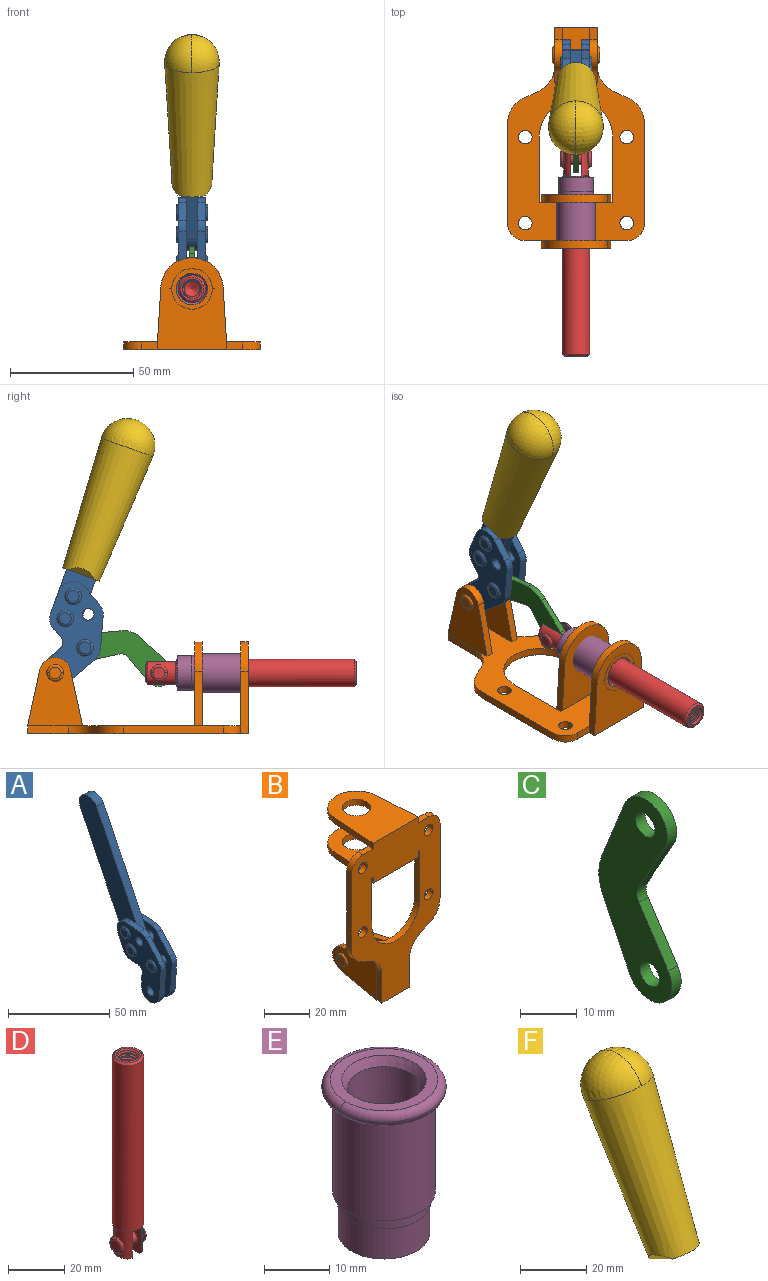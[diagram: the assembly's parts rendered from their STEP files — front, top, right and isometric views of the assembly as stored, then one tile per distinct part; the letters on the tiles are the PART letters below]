
ASSEMBLY  parts=6 mates=6
PART A: 59 faces, bbox 12.9x60.2x99.6 mm
  f0: torus R=2.39mm, axis (-1,0,0), area 14.9mm2, adj f20,f43,f51
  f1: torus R=2.39mm, axis (-1,0,0), area 14.9mm2, adj f19,f42,f51
  f2: torus R=2.39mm, axis (-1,0,0), area 14.9mm2, adj f18,f35,f51
  f3: torus R=2.39mm, axis (-1,0,0), area 14.9mm2, adj f14,f17,f23
  f4: torus R=2.39mm, axis (-1,0,0), area 14.9mm2, adj f13,f16,f23
  f5: torus R=2.39mm, axis (-1,0,0), area 14.9mm2, adj f12,f15,f23
  f6: cylinder r=2.39mm len=4.78mm, axis (1,0,0), area 46.5mm2, adj f48,f50,f51
  f7: cylinder r=2.39mm len=4.78mm, axis (1,0,0), area 46.5mm2, adj f50,f51
  f8: cylinder r=6.35mm len=12.68mm, axis (1,0,0), area 61.8mm2, adj f38,f39,f50,f51
  f9: cylinder r=2.39mm len=4.78mm, axis (-1,0,0), area 70.5mm2, adj f46,f50
  f10: cylinder r=2.39mm len=4.78mm, axis (-1,0,0), area 46.5mm2, adj f23,f45,f46
  f11: cylinder r=2.39mm len=4.78mm, axis (-1,0,0), area 46.5mm2, adj f23,f46
  f12: plane 4.78x4.78mm, normal (1,0,0), area 17.9mm2, adj f5,f15
  f13: plane 4.78x4.78mm, normal (1,0,0), area 17.9mm2, adj f4,f16
  f14: plane 4.78x4.78mm, normal (1,0,0), area 17.9mm2, adj f3,f17
  f15: torus R=2.39mm, axis (-1,0,0), area 14.9mm2, adj f5,f12,f23
  f16: torus R=2.39mm, axis (-1,0,0), area 14.9mm2, adj f4,f13,f23
  f17: torus R=2.39mm, axis (-1,0,0), area 14.9mm2, adj f3,f14,f23
  f18: plane 4.78x4.78mm, normal (-1,0,0), area 17.9mm2, adj f2,f35
  f19: plane 4.78x4.78mm, normal (-1,0,0), area 17.9mm2, adj f1,f42
  f20: plane 4.78x4.78mm, normal (-1,0,0), area 17.9mm2, adj f0,f43
  f21: plane 2.26x0.2mm, normal (1,0,0), area 0.2mm2, adj f31,f44
  f22: plane 2.26x0.2mm, normal (-1,0,0), area 0.2mm2, adj f41,f44
  f23: plane 39.37x30.77mm, normal (1,0,0), area 565.5mm2, adj f3,f4,f5,f10,f11,f15,f16,f17
  f24: cylinder r=6.1mm len=4.15mm, axis (-1,0,0), area 14.7mm2, adj f23,f25,f32,f46
  f25: plane 10.25x9.01mm, normal (0,-0.75,0.66), area 42.3mm2, adj f23,f24,f26,f46
  f26: cylinder r=6.35mm len=4.64mm, axis (-1,0,0), area 15.6mm2, adj f23,f25,f27,f46
  f27: plane 15.84x3.1mm, normal (0,-1,-0.07), area 49.2mm2, adj f23,f26,f28,f46
  f28: cylinder r=6.35mm len=12.68mm, axis (-1,0,0), area 61.8mm2, adj f23,f27,f29,f46
  f29: plane 8.11x3.1mm, normal (0,1,0.07), area 25.2mm2, adj f23,f28,f30,f46
  f30: cylinder r=3.05mm len=3.25mm, axis (-1,0,0), area 14.8mm2, adj f23,f29,f31,f46
  f31: plane 5.99x3.1mm, normal (0,0.07,-1), area 18.6mm2, adj f21,f23,f30,f44,f46
  f32: plane 9.5x3.1mm, normal (0,-0.07,1), area 29.5mm2, adj f23,f24,f33,f46,f47
  f33: cylinder r=6.1mm len=8.63mm, axis (-1,0,0), area 39.1mm2, adj f23,f32,f34,f47
  f34: plane 8.65x3.96mm, normal (0,0.91,-0.42), area 29.5mm2, adj f23,f33,f44,f47
  f35: torus R=2.39mm, axis (-1,0,0), area 14.9mm2, adj f2,f18,f51
  f36: plane 10.25x9.01mm, normal (0,-0.75,0.66), area 42.3mm2, adj f37,f49,f50,f51
  f37: cylinder r=6.35mm len=4.64mm, axis (1,0,0), area 15.6mm2, adj f36,f38,f50,f51
  f38: plane 15.84x3.1mm, normal (0,-1,-0.07), area 49.2mm2, adj f8,f37,f50,f51
  f39: plane 8.11x3.1mm, normal (0,1,0.07), area 25.2mm2, adj f8,f40,f50,f51
  f40: cylinder r=3.05mm len=3.25mm, axis (1,0,0), area 14.8mm2, adj f39,f41,f50,f51
  f41: plane 5.99x3.1mm, normal (0,0.07,-1), area 18.6mm2, adj f22,f40,f44,f50,f51
  f42: torus R=2.39mm, axis (-1,0,0), area 14.9mm2, adj f1,f19,f51
  f43: torus R=2.39mm, axis (-1,0,0), area 14.9mm2, adj f0,f20,f51
  f44: cylinder r=6.35mm len=12.12mm, axis (-1,0,0), area 128.9mm2, adj f21,f22,f23,f31,f34,f41,f46,f47
  f45: plane 2.65x1.35mm, normal (1,0,0), area 1mm2, adj f10,f55
  f46: plane 39.08x20.42mm, normal (-1,0,0), area 412.5mm2, adj f9,f10,f11,f24,f25,f26,f27,f28
  f47: plane 77.62x39.82mm, normal (1,0,0), area 850mm2, adj f32,f33,f34,f44,f53,f54,f55
  f48: plane 2.65x1.35mm, normal (-1,0,0), area 1mm2, adj f6,f55
  f49: cylinder r=6.1mm len=4.15mm, axis (1,0,0), area 14.7mm2, adj f36,f50,f51,f56
  f50: plane 39.08x20.42mm, normal (1,0,0), area 412.5mm2, adj f6,f7,f8,f9,f36,f37,f38,f39
  f51: plane 39.37x30.77mm, normal (-1,0,0), area 565.5mm2, adj f0,f1,f2,f6,f7,f8,f35,f36
  f52: plane 8.65x3.96mm, normal (0,0.91,-0.42), area 29.5mm2, adj f44,f51,f57,f58
  f53: plane 68.49x33.4mm, normal (0,0.9,-0.44), area 358.1mm2, adj f44,f47,f54,f58
  f54: cylinder r=6.35mm len=12.06mm, axis (1,0,0), area 93.7mm2, adj f47,f53,f55,f58
  f55: plane 68.49x33.4mm, normal (0,-0.9,0.44), area 358.1mm2, adj f44,f45,f46,f47,f48,f50,f54,f58
  f56: plane 9.5x3.1mm, normal (0,-0.07,1), area 29.5mm2, adj f49,f50,f51,f57,f58
  f57: cylinder r=6.1mm len=8.63mm, axis (1,0,0), area 39.1mm2, adj f51,f52,f56,f58
  f58: plane 77.62x39.82mm, normal (-1,0,0), area 850mm2, adj f44,f52,f53,f54,f55,f56,f57
PART B: 55 faces, bbox 55.7x37.4x89.8 mm
  f0: torus R=2.41mm, axis (-1,0,0), area 15mm2, adj f11,f15,f25
  f1: torus R=2.41mm, axis (-1,0,0), area 15mm2, adj f10,f12,f22
  f2: cylinder r=2.78mm len=5.56mm, axis (0,-1,0), area 54.2mm2, adj f30,f54
  f3: cylinder r=14.99mm len=29.97mm, axis (0,-1,0), area 145.9mm2, adj f30,f49,f53,f54
  f4: cylinder r=2.78mm len=5.56mm, axis (0,-1,0), area 54.2mm2, adj f30,f54
  f5: cylinder r=2.78mm len=5.56mm, axis (0,-1,0), area 54.2mm2, adj f30,f54
  f6: cylinder r=2.78mm len=5.56mm, axis (0,-1,0), area 54.2mm2, adj f30,f54
  f7: cylinder r=6.35mm len=12.7mm, axis (0,0,1), area 123.6mm2, adj f27,f51
  f8: cylinder r=6.35mm len=12.7mm, axis (0,0,-1), area 124.7mm2, adj f21,f35
  f9: cylinder r=2.41mm len=11.18mm, axis (-1,0,0), area 169.4mm2, adj f16,f19
  f10: plane 4.83x4.83mm, normal (1,0,0), area 18.3mm2, adj f1,f12
  f11: plane 4.83x4.83mm, normal (-1,0,0), area 18.3mm2, adj f0,f15
  f12: torus R=2.41mm, axis (-1,0,0), area 15mm2, adj f1,f10,f22
  f13: cylinder r=6.35mm len=12.41mm, axis (1,0,0), area 53.4mm2, adj f18,f19,f22,f23
  f14: cylinder r=6.35mm len=12.41mm, axis (-1,0,0), area 53.4mm2, adj f16,f17,f24,f25
  f15: torus R=2.41mm, axis (-1,0,0), area 15mm2, adj f0,f11,f25
  f16: plane 27.86x22.35mm, normal (1,0,0), area 425.4mm2, adj f9,f14,f17,f24,f30
  f17: plane 22.86x4.97mm, normal (0,0.21,0.98), area 72.5mm2, adj f14,f16,f25,f30
  f18: plane 22.86x4.97mm, normal (0,0.21,0.98), area 72.5mm2, adj f13,f19,f22,f30
  f19: plane 27.86x22.35mm, normal (-1,0,0), area 425.4mm2, adj f9,f13,f18,f23,f30
  f20: cylinder r=12.7mm len=25.35mm, axis (0,0,-1), area 119.8mm2, adj f21,f34,f35,f36
  f21: plane 34.21x28.07mm, normal (0,0,-1), area 702.4mm2, adj f8,f20,f30,f34,f36
  f22: plane 27.96x22.45mm, normal (1,0,0), area 407.2mm2, adj f1,f12,f13,f18,f23,f30,f42,f43
  f23: plane 22.86x4.97mm, normal (0,0.21,-0.98), area 72.5mm2, adj f13,f19,f22,f44
  f24: plane 22.86x4.97mm, normal (0,0.21,-0.98), area 72.5mm2, adj f14,f16,f25,f44
  f25: plane 27.86x22.35mm, normal (-1,0,0), area 407.1mm2, adj f0,f14,f15,f17,f24,f30,f45,f46
  f26: plane 3.1x0.95mm, normal (0,0,-1), area 2.7mm2, adj f30,f49,f50,f54
  f27: plane 34.21x28.07mm, normal (0,0,1), area 702.4mm2, adj f7,f28,f30,f50,f52
  f28: cylinder r=12.7mm len=25.35mm, axis (0,0,1), area 118.8mm2, adj f27,f50,f51,f52
  f29: plane 3.1x0.95mm, normal (0,0,-1), area 2.7mm2, adj f30,f52,f53,f54
  f30: plane 86.54x55.63mm, normal (0,1,0), area 2362.9mm2, adj f2,f3,f4,f5,f6,f16,f17,f18
  f31: plane 40.56x3.1mm, normal (-1,0,0), area 125.7mm2, adj f30,f32,f48,f54
  f32: cylinder r=7.11mm len=7.11mm, axis (0,-1,0), area 34.6mm2, adj f30,f31,f33,f54
  f33: plane 6.67x3.1mm, normal (0,0,1), area 20.4mm2, adj f30,f32,f34,f54
  f34: plane 25.39x3.13mm, normal (-1,0.06,0), area 79.5mm2, adj f20,f21,f33,f35,f54
  f35: plane 37.31x28.45mm, normal (0,0,1), area 789.9mm2, adj f8,f20,f34,f36,f54
  f36: plane 25.39x3.13mm, normal (1,0.06,0), area 79.5mm2, adj f20,f21,f35,f37,f54
  f37: plane 6.67x3.1mm, normal (0,0,1), area 20.4mm2, adj f30,f36,f38,f54
  f38: cylinder r=7.11mm len=7.11mm, axis (0,-1,0), area 34.6mm2, adj f30,f37,f39,f54
  f39: plane 40.56x3.1mm, normal (1,0,0), area 125.7mm2, adj f30,f38,f40,f54
  f40: cylinder r=11.18mm len=10.16mm, axis (0,-1,0), area 39.5mm2, adj f30,f39,f41,f54
  f41: plane 6.09x3.1mm, normal (0.42,0,-0.91), area 20.8mm2, adj f30,f40,f42,f54
  f42: cylinder r=11.18mm len=9.41mm, axis (0,-1,0), area 37.2mm2, adj f22,f30,f41,f43,f54
  f43: plane 16.5x3.1mm, normal (1,0,0), area 51.1mm2, adj f22,f42,f44,f54
  f44: plane 17.37x3.1mm, normal (0,0,-1), area 53.8mm2, adj f23,f24,f30,f43,f45,f54
  f45: plane 16.5x3.1mm, normal (-1,0,0), area 51.1mm2, adj f25,f44,f46,f54
  f46: cylinder r=11.18mm len=9.41mm, axis (0,-1,0), area 37.2mm2, adj f25,f30,f45,f47,f54
  f47: plane 6.09x3.1mm, normal (-0.42,0,-0.91), area 20.8mm2, adj f30,f46,f48,f54
  f48: cylinder r=11.18mm len=10.16mm, axis (0,-1,0), area 39.5mm2, adj f30,f31,f47,f54
  f49: plane 26.54x3.1mm, normal (-1,0,0), area 82.3mm2, adj f3,f26,f30,f54
  f50: plane 25.39x3.1mm, normal (1,0.06,0), area 78.8mm2, adj f26,f27,f28,f51,f54
  f51: plane 37.31x28.45mm, normal (0,0,-1), area 789.9mm2, adj f7,f28,f50,f52,f54
  f52: plane 25.39x3.1mm, normal (-1,0.06,0), area 78.8mm2, adj f27,f28,f29,f51,f54
  f53: plane 26.54x3.1mm, normal (1,0,0), area 82.3mm2, adj f3,f29,f30,f54
  f54: plane 89.66x55.63mm, normal (0,-1,0), area 2678.5mm2, adj f2,f3,f4,f5,f6,f26,f29,f31
PART C: 12 faces, bbox 2.3x18.2x42.8 mm
  f0: cylinder r=2.4mm len=4.8mm, axis (1,0,0), area 34.9mm2, adj f4,f11
  f1: cylinder r=10.41mm len=8.47mm, axis (1,0,0), area 20.2mm2, adj f4,f9,f10,f11
  f2: cylinder r=3.05mm len=3.16mm, axis (1,0,0), area 7.7mm2, adj f4,f6,f7,f11
  f3: cylinder r=2.4mm len=4.8mm, axis (1,0,0), area 34.9mm2, adj f4,f11
  f4: plane 42.81x18.23mm, normal (-1,0,0), area 414.1mm2, adj f0,f1,f2,f3,f5,f6,f7,f8
  f5: cylinder r=5.54mm len=10.67mm, axis (1,0,0), area 41.8mm2, adj f4,f6,f10,f11
  f6: plane 11.66x6.53mm, normal (0,-0.87,-0.49), area 30.9mm2, adj f2,f4,f5,f11
  f7: plane 11.17x7.33mm, normal (0,-0.84,0.55), area 30.9mm2, adj f2,f4,f8,f11
  f8: cylinder r=5.54mm len=10.51mm, axis (1,0,0), area 41.8mm2, adj f4,f7,f9,f11
  f9: plane 13.67x6.67mm, normal (0,0.9,-0.44), area 35.1mm2, adj f1,f4,f8,f11
  f10: plane 14.1x5.7mm, normal (0,0.93,0.37), area 35.1mm2, adj f1,f4,f5,f11
  f11: plane 42.81x18.23mm, normal (1,0,0), area 414.1mm2, adj f0,f1,f2,f3,f5,f6,f7,f8
PART D: 48 faces, bbox 12.6x11.1x86.1 mm
  f0: torus R=2.41mm, axis (-1,0,0), area 15mm2, adj f30,f32,f34
  f1: torus R=2.41mm, axis (-1,0,0), area 15mm2, adj f29,f31,f33
  f2: cylinder r=5.54mm len=72.39mm, axis (0,0,1), area 2518.5mm2, adj f3,f4,f42,f43
  f3: cone r=5.54mm half-angle=45deg, axis (0,0,1), area 7.6mm2, adj f2,f5,f41
  f4: cone r=5.54mm half-angle=45deg, axis (0,0,-1), area 34.9mm2, adj f2,f39
  f5: cylinder r=5.08mm len=11.48mm, axis (0,0,1), area 108.3mm2, adj f3,f7,f8,f41
  f6: cylinder r=2.41mm len=4.83mm, axis (-1,0,0), area 71.2mm2, adj f40,f41
  f7: cylinder r=2.41mm len=4.83mm, axis (-1,0,0), area 7.6mm2, adj f5,f34
  f8: cone r=5.08mm half-angle=45deg, axis (0,0,1), area 10.6mm2, adj f5,f37,f41
  f9: cone r=3.98mm half-angle=45deg, axis (0,0,1), area 17.6mm2, adj f27,f39,f45,f46,f47
  f10: cylinder r=2.41mm len=4.83mm, axis (-1,0,0), area 7.6mm2, adj f33,f38
  f11: cylinder r=3.2mm len=6.4mm, axis (0,0,1), area 78.4mm2, adj f12,f28,f44,f45,f47
  f12: cylinder r=3.2mm len=6.4mm, axis (0,0,1), area 10.5mm2, adj f11,f13,f45,f47
  f13: cylinder r=3.2mm len=6.4mm, axis (0,0,1), area 10.5mm2, adj f12,f14,f45,f47
  f14: cylinder r=3.2mm len=6.4mm, axis (0,0,1), area 10.5mm2, adj f13,f15,f45,f47
  f15: cylinder r=3.2mm len=6.4mm, axis (0,0,1), area 10.5mm2, adj f14,f16,f45,f47
  f16: cylinder r=3.2mm len=6.4mm, axis (0,0,1), area 10.5mm2, adj f15,f17,f45,f47
  f17: cylinder r=3.2mm len=6.4mm, axis (0,0,1), area 10.5mm2, adj f16,f18,f45,f47
  f18: cylinder r=3.2mm len=6.4mm, axis (0,0,1), area 10.5mm2, adj f17,f19,f45,f47
  f19: cylinder r=3.2mm len=6.4mm, axis (0,0,1), area 10.5mm2, adj f18,f20,f45,f47
  f20: cylinder r=3.2mm len=6.4mm, axis (0,0,1), area 10.5mm2, adj f19,f21,f45,f47
  f21: cylinder r=3.2mm len=6.4mm, axis (0,0,1), area 10.5mm2, adj f20,f22,f45,f47
  f22: cylinder r=3.2mm len=6.4mm, axis (0,0,1), area 10.5mm2, adj f21,f23,f45,f47
  f23: cylinder r=3.2mm len=6.4mm, axis (0,0,1), area 10.5mm2, adj f22,f24,f45,f47
  f24: cylinder r=3.2mm len=6.4mm, axis (0,0,1), area 10.5mm2, adj f23,f25,f45,f47
  f25: cylinder r=3.2mm len=6.4mm, axis (0,0,1), area 10.5mm2, adj f24,f26,f45,f47
  f26: cylinder r=3.2mm len=6.4mm, axis (0,0,1), area 10.5mm2, adj f25,f27,f45,f47
  f27: cylinder r=3.2mm len=6.4mm, axis (0,0,1), area 7.4mm2, adj f9,f26,f45,f47
  f28: cone r=3.2mm half-angle=60deg, axis (0,0,1), area 37.2mm2, adj f11
  f29: plane 4.83x4.83mm, normal (-1,0,0), area 18.3mm2, adj f1,f31
  f30: plane 4.83x4.83mm, normal (1,0,0), area 18.3mm2, adj f0,f32
  f31: torus R=2.41mm, axis (-1,0,0), area 15mm2, adj f1,f29,f33
  f32: torus R=2.41mm, axis (-1,0,0), area 15mm2, adj f0,f30,f34
  f33: plane 6.83x6.83mm, normal (1,0,0), area 18.3mm2, adj f1,f10,f31
  f34: plane 6.83x6.83mm, normal (-1,0,0), area 18.3mm2, adj f0,f7,f32
  f35: cone r=5.08mm half-angle=45deg, axis (0,0,1), area 10.6mm2, adj f36,f38,f40
  f36: plane 7.25x1.97mm, normal (0,0,-1), area 10mm2, adj f35,f40
  f37: plane 7.25x1.97mm, normal (0,0,-1), area 10mm2, adj f8,f41
  f38: cylinder r=5.08mm len=11.48mm, axis (0,0,1), area 108.3mm2, adj f10,f35,f40,f42
  f39: plane 9.55x9.55mm, normal (0,0,1), area 22mm2, adj f4,f9
  f40: plane 12.76x10.09mm, normal (1,0,0), area 95.7mm2, adj f6,f35,f36,f38,f42,f43
  f41: plane 12.76x10.09mm, normal (-1,0,0), area 95.7mm2, adj f3,f5,f6,f8,f37,f43
  f42: cone r=5.54mm half-angle=45deg, axis (0,0,1), area 7.6mm2, adj f2,f38,f40
  f43: plane 11.07x4.7mm, normal (0,0,-1), area 50.4mm2, adj f2,f40,f41
  f44: plane 0.89x0.62mm, normal (-1,0,0), area 0.3mm2, adj f11,f45,f46,f47
  f45: bspline ~24.8x7.63mm, area 266.6mm2, adj f9,f11,f12,f13,f14,f15,f16,f17
  f46: bspline ~24.87x7.63mm, area 73.6mm2, adj f9,f44,f45,f47
  f47: bspline ~24.98x7.63mm, area 272.5mm2, adj f9,f11,f12,f13,f14,f15,f16,f17
PART E: 15 faces, bbox 20.6x20.6x28.7 mm
  f0: torus R=8.26mm, axis (0,0,1), area 56.8mm2, adj f1,f10,f12
  f1: torus R=8.26mm, axis (0,0,1), area 56.8mm2, adj f0,f6,f13
  f2: cylinder r=5.59mm len=25.91mm, axis (0,0,1), area 909.6mm2, adj f3,f4
  f3: cone r=6.86mm half-angle=45deg, axis (0,0,-1), area 70.2mm2, adj f2,f14
  f4: cone r=6.47mm half-angle=30deg, axis (0,0,1), area 66.7mm2, adj f2,f13
  f5: cylinder r=7.04mm len=14.07mm, axis (0,0,1), area 252.6mm2, adj f11,f14
  f6: torus R=8.26mm, axis (0,0,1), area 56.8mm2, adj f1,f12,f13
  f7: cylinder r=7.16mm len=14.33mm, axis (0,0,1), area 91.5mm2, adj f9,f11
  f8: cylinder r=7.86mm len=18.42mm, axis (0,0,1), area 909.6mm2, adj f9,f10
  f9: plane 15.72x15.72mm, normal (0,0,-1), area 33mm2, adj f7,f8
  f10: plane 16.51x16.51mm, normal (0,0,-1), area 19.9mm2, adj f0,f8,f12
  f11: plane 14.33x14.33mm, normal (0,0,-1), area 5.7mm2, adj f5,f7
  f12: torus R=8.26mm, axis (0,0,1), area 56.8mm2, adj f0,f6,f10
  f13: plane 16.51x16.51mm, normal (0,0,1), area 82.7mm2, adj f1,f4,f6
  f14: plane 14.07x14.07mm, normal (0,0,-1), area 7.8mm2, adj f3,f5
PART F: 11 faces, bbox 22.3x42.6x64.5 mm
  f0: sphere r=11.13mm, area 411.4mm2, adj f1,f8
  f1: cone r=11.11mm half-angle=3.3deg, axis (0,0.44,0.9), area 3251.8mm2, adj f0,f7,f8,f9,f10
  f2: cylinder r=6.16mm len=11.7mm, axis (1,0,0), area 89.5mm2, adj f3,f4,f5,f6
  f3: plane 60.23x36.75mm, normal (-1,0,0), area 763.6mm2, adj f2,f4,f6,f10
  f4: plane 51.37x25.05mm, normal (0,0.9,-0.44), area 264.2mm2, adj f2,f3,f5,f10
  f5: plane 60.23x36.75mm, normal (1,0,0), area 763.6mm2, adj f2,f4,f6,f10
  f6: plane 51.37x25.05mm, normal (0,-0.9,0.44), area 264.2mm2, adj f2,f3,f5,f10
  f7: plane 9.95x5.95mm, normal (0.71,-0.31,-0.64), area 25.8mm2, adj f1,f10
  f8: sphere r=11.13mm, area 411.4mm2, adj f0,f1
  f9: plane 9.95x5.95mm, normal (-0.71,-0.31,-0.64), area 25.8mm2, adj f1,f10
  f10: plane 14.27x11.38mm, normal (0,-0.44,-0.9), area 106.7mm2, adj f1,f3,f4,f5,f6,f7,f9
PLACE A rot(axis=(1,0,0),45.9deg) t=(0,1.06,29.3)mm
PLACE B rot(axis=(1,0,0),90deg) t=(0,9.14,0)mm fixed
PLACE C rot(axis=(1,0,0),110.8deg) t=(0,22.25,7.1)mm
PLACE D rot(axis=(1,0,0),90deg) t=(0,14.51,0)mm
PLACE E rot(axis=(1,0,0),90deg) t=(0,11.68,0)mm
PLACE F rot(axis=(1,0,0),45.9deg) t=(-0.04,1.06,29.3)mm
MATE slider E.f2 <-> D.f2  axis (0,1,0) through (0,-35.73,24.61)mm
MATE revolute A.f4 <-> C.f3  axis (-1,0,0) through (0,29.1,34.85)mm
MATE fastened E.f12 <-> B.f7  axis (0,-1,0) through (0,-37.25,24.61)mm
MATE revolute B.f0 <-> A.f7  axis (-1,0,0) through (0,41.23,24.61)mm
MATE revolute C.f5 <-> D.f6  axis (1,0,0) through (0,-0.96,24.61)mm
MATE fastened F.f2 <-> A.f54  axis (1,0,0) through (-2.35,11.22,118.42)mm
